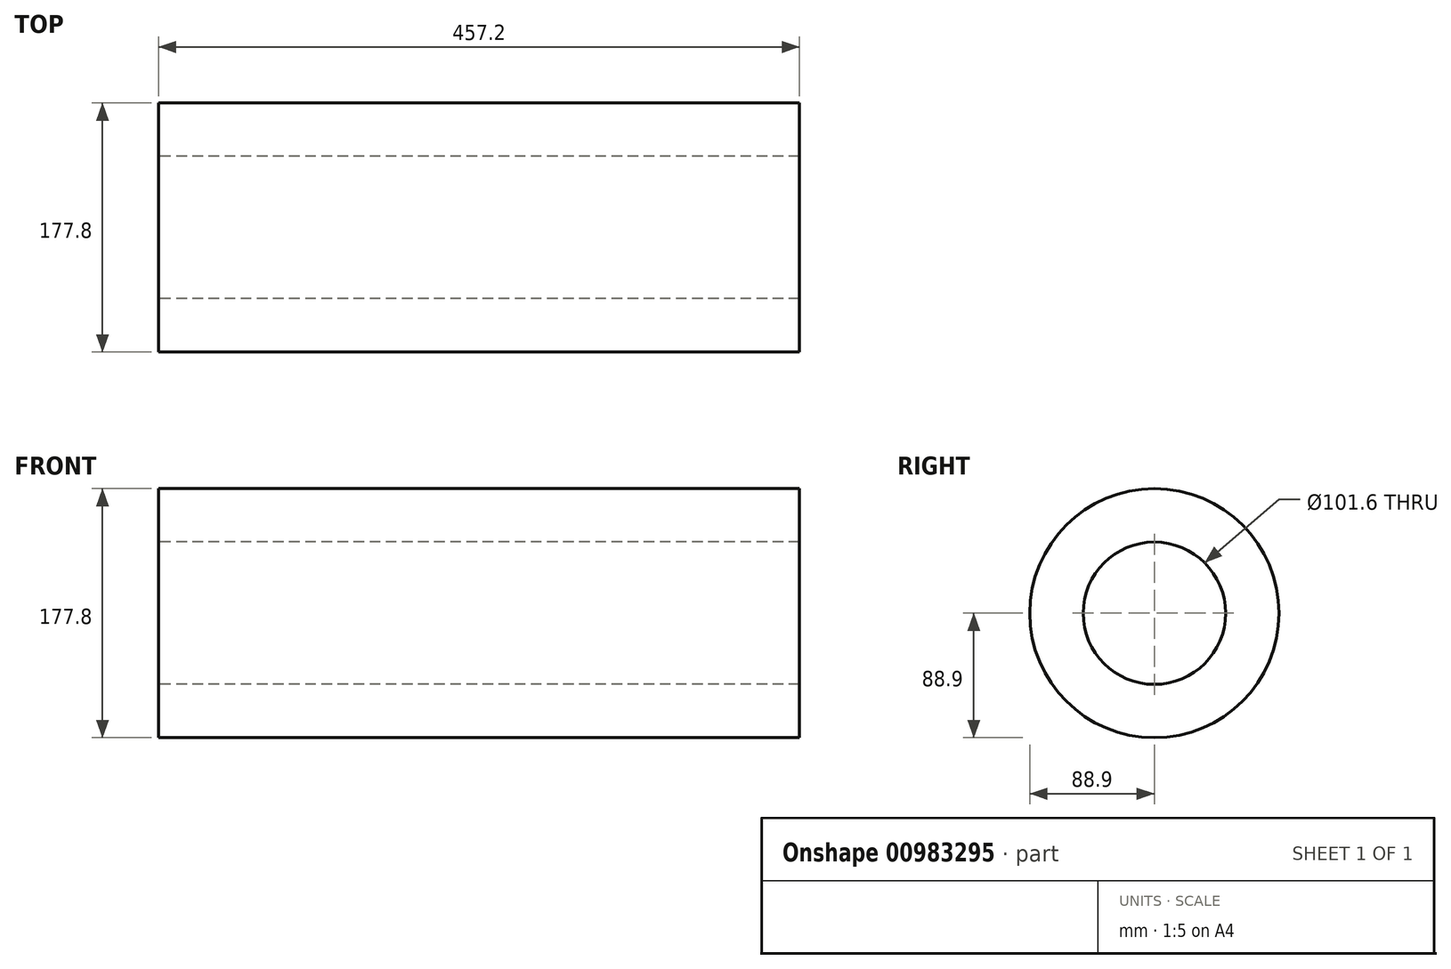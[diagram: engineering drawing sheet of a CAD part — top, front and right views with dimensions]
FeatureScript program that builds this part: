
annotation { "Feature Type Name" : "Feature", "Feature Type Description" : "" }
export const myFeature = defineFeature(function(context is Context, id is Id, definition is map)
    precondition{}
    {
        {
            var Q0;
            Q0=qCreatedBy(makeId("Right.planeOp"),FACE);
            var sketch = newSketch(context, id + "F0", { "sketchPlane" : qUnion([Q0])});
            skCircle(sketch, "E0", {"center": v(0, 0) * mm, "radius": 50.8 * mm});
            skCircle(sketch, "E1", {"center": v(0, 0) * mm, "radius": 88.9 * mm});
            skSolve(sketch);
        }
        {
            var Q0;
            Q0=makeQuery(id+"F0.imprint","IMPRINT",FACE,{"disambiguationData":[TD([[makeQuery(id+"F0.imprint","IMPRINT",EDGE,{"derivedFrom":sQuery(id+"F0.wireOp",EDGE,"E0")}),-1.0]])]});
            extrude(context, id + "F1", {"entities" : qUnion([Q0]), "depth" : 457.2 * mm, "offsetDistance" : 25.4 * mm});
        }
    });
